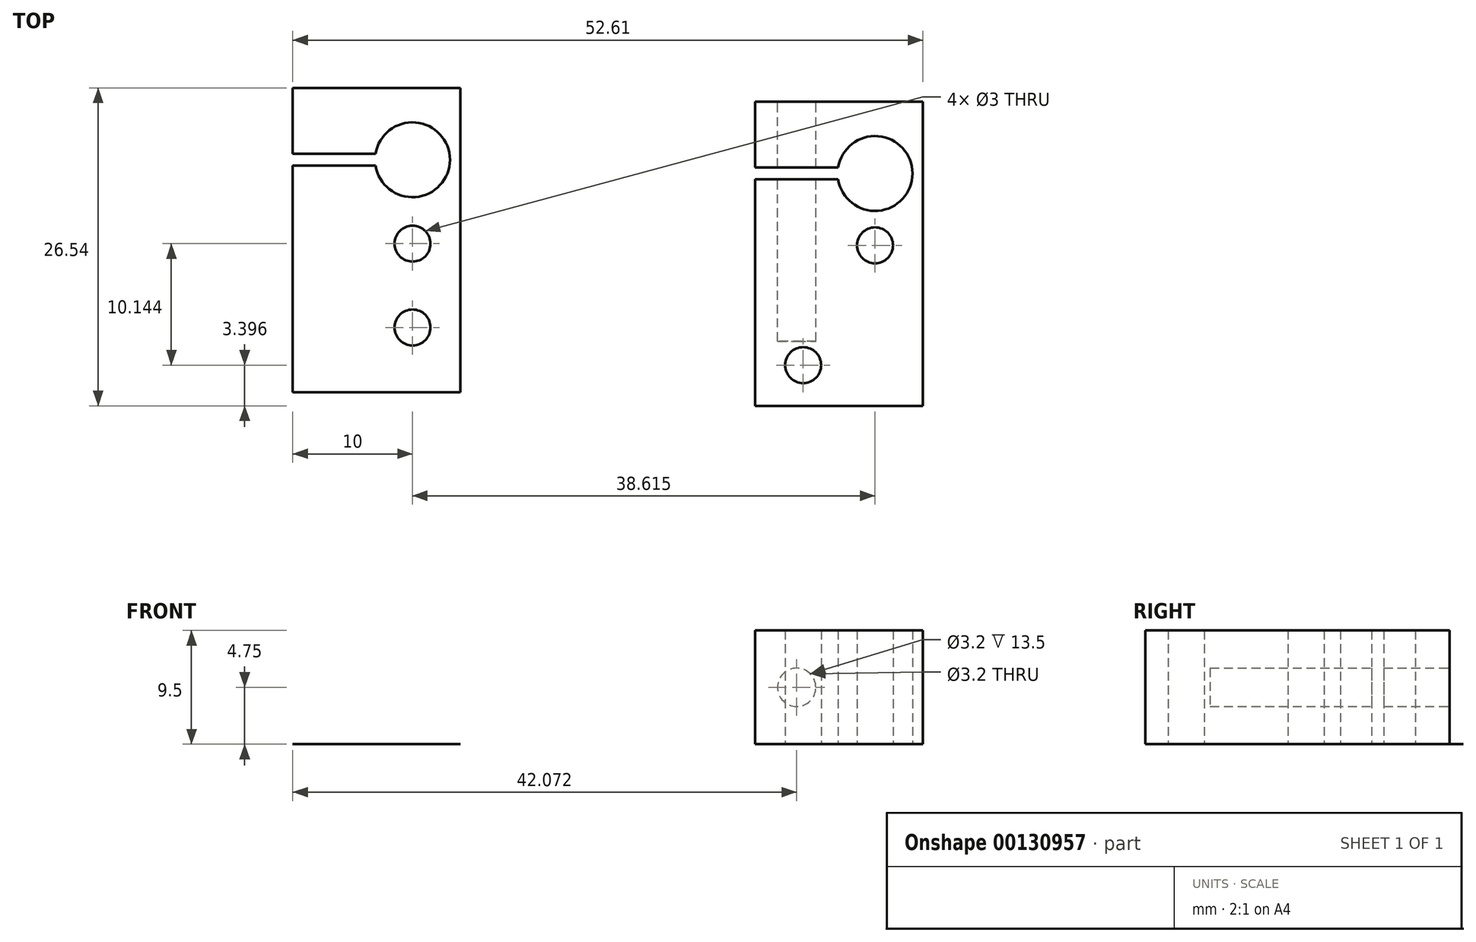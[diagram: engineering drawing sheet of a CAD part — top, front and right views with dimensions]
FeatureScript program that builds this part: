
annotation { "Feature Type Name" : "Feature", "Feature Type Description" : "" }
export const myFeature = defineFeature(function(context is Context, id is Id, definition is map)
    precondition{}
    {
        {
            var Q0;
            Q0=qCreatedBy(makeId("Top.planeOp"),FACE);
            var sketch = newSketch(context, id + "F0", { "sketchPlane" : qUnion([Q0])});
            skLineSegment(sketch, "E0.bottom", {"start": v(7, -12.7) * mm, "end": v(-7, -12.7) * mm});
            skLineSegment(sketch, "E0.top", {"start": v(7, 12.7) * mm, "end": v(-7, 12.7) * mm});
            skLineSegment(sketch, "E0.left", {"start": v(7, -12.7) * mm, "end": v(7, 12.7) * mm});
            skLineSegment(sketch, "E0.right", {"start": v(-7, -12.7) * mm, "end": v(-7, 6.2) * mm});
            skPoint(sketch, "E0.middle", {"position": v(0, 0) * mm});
            skArc(sketch, "E1", {"start": v(-0.08, 6.2) * mm, "mid": v(6.12, 6.7) * mm, "end": v(-0.08, 7.2) * mm});
            skCircle(sketch, "E2", {"center": v(3, -7.3) * mm, "radius": 1.5 * mm});
            skLineSegment(sketch, "E3.bottom", {"start": v(-5, 12.7) * mm, "end": v(-2, 12.7) * mm, "construction": true});
            skLineSegment(sketch, "E3.top", {"start": v(-5, -12.7) * mm, "end": v(-2, -12.7) * mm, "construction": true});
            skLineSegment(sketch, "E3.left", {"start": v(-5, 12.7) * mm, "end": v(-5, -12.7) * mm, "construction": true});
            skLineSegment(sketch, "E3.right", {"start": v(-2, 12.7) * mm, "end": v(-2, -12.7) * mm, "construction": true});
            skLineSegment(sketch, "E4.bottom", {"start": v(-7, 7.2) * mm, "end": v(-0.08, 7.2) * mm});
            skLineSegment(sketch, "E4.top", {"start": v(-7, 6.2) * mm, "end": v(-0.08, 6.2) * mm});
            skLineSegment(sketch, "E5.trimOffspring", {"start": v(-7, 7.2) * mm, "end": v(-7, 12.7) * mm});
            skLineSegment(sketch, "E6", {"start": v(-3.54, 6.2) * mm, "end": v(-3.54, 7.2) * mm, "construction": true});
            skCircle(sketch, "E7", {"center": v(3, -0.3) * mm, "radius": 1.5 * mm});
            skLineSegment(sketch, "E8", {"start": v(3, -7.3) * mm, "end": v(3, -0.3) * mm, "construction": true});
            skLineSegment(sketch, "E9", {"start": v(3, -0.3) * mm, "end": v(3, 6.7) * mm, "construction": true});
            skSolve(sketch);
        }
        {
            var Q0;
            Q0=qSketchRegion(id+"F0",true);
            extrude(context, id + "F1", {"entities" : qUnion([Q0]), "depth" : 3 / 203.2 * mm});
        }
        {
            var Q0;
            Q0=makeQuery(id+"F1.opExtrude","SWEPT_FACE",FACE,{"disambiguationData":[OSD([sQuery(id+"F0.wireOp",EDGE,"E0.top")])]});
            var sketch = newSketch(context, id + "F2", { "sketchPlane" : qUnion([Q0])});
            skCircle(sketch, "E10", {"center": v(3.54, 4.76) * mm, "radius": 1.25 * mm});
            skLineSegment(sketch, "E11", {"start": v(7, 4.76) * mm, "end": v(0.08, 4.76) * mm, "construction": true});
            skSolve(sketch);
        }
        {
            var Q0;
            Q0=qSketchRegion(id+"F2",true);
            extrude(context, id + "F3", {"entities" : qUnion([Q0]), "operationType" : NewBodyOperationType.REMOVE, "endBound" : BoundingType.THROUGH_ALL, "oppositeDirection" : true, "depth" : 25 * mm});
        }
        {
            var Q0;
            Q0=qCreatedBy(makeId("Top.planeOp"),FACE);
            var sketch = newSketch(context, id + "F4", { "sketchPlane" : qUnion([Q0])});
            skLineSegment(sketch, "E12.bottom", {"start": v(45.61, -13.84) * mm, "end": v(31.61, -13.84) * mm});
            skLineSegment(sketch, "E12.top", {"start": v(45.61, 11.56) * mm, "end": v(31.61, 11.56) * mm});
            skLineSegment(sketch, "E12.left", {"start": v(45.61, -13.84) * mm, "end": v(45.61, 11.56) * mm});
            skLineSegment(sketch, "E12.right", {"start": v(31.61, -13.84) * mm, "end": v(31.61, 5.06) * mm});
            skPoint(sketch, "E12.middle", {"position": v(38.61, -1.14) * mm});
            skArc(sketch, "E13", {"start": v(38.53, 5.06) * mm, "mid": v(44.74, 5.56) * mm, "end": v(38.53, 6.06) * mm});
            skCircle(sketch, "E14", {"center": v(35.61, -10.44) * mm, "radius": 1.5 * mm});
            skLineSegment(sketch, "E15.bottom", {"start": v(31.61, 6.06) * mm, "end": v(38.53, 6.06) * mm});
            skLineSegment(sketch, "E15.top", {"start": v(31.61, 5.06) * mm, "end": v(38.53, 5.06) * mm});
            skLineSegment(sketch, "E16.trimOffspring", {"start": v(31.61, 6.06) * mm, "end": v(31.61, 11.56) * mm});
            skLineSegment(sketch, "E17", {"start": v(35.07, 5.06) * mm, "end": v(35.07, 6.06) * mm, "construction": true});
            skCircle(sketch, "E18", {"center": v(41.61, -0.44) * mm, "radius": 1.5 * mm});
            skLineSegment(sketch, "E19", {"start": v(35.61, -10.44) * mm, "end": v(35.61, -13.84) * mm, "construction": true});
            skLineSegment(sketch, "E20", {"start": v(35.61, -10.44) * mm, "end": v(41.61, -10.44) * mm, "construction": true});
            skLineSegment(sketch, "E21", {"start": v(41.61, -10.44) * mm, "end": v(41.61, -0.44) * mm, "construction": true});
            skSolve(sketch);
        }
        {
            var Q0;
            Q0 = qSketchRegion(id + "F4", true);
            extrude(context, id + "F5", {"entities" : qUnion([Q0]), "depth" : 9.5 * mm});
        }
        {
            var Q0;
            Q0=makeQuery(id+"F5.opExtrude","SWEPT_FACE",FACE,{"disambiguationData":[OSD([sQuery(id+"F4.wireOp",EDGE,"E12.top")])]});
            var sketch = newSketch(context, id + "F6", { "sketchPlane" : qUnion([Q0])});
            skLineSegment(sketch, "E22", {"start": v(-38.53, 4.75) * mm, "end": v(-31.61, 4.75) * mm, "construction": true});
            skCircle(sketch, "E23", {"center": v(-35.07, 4.75) * mm, "radius": 1.6 * mm});
            skSolve(sketch);
        }
        {
            var Q0;
            Q0 = qSketchRegion(id + "F6", true);
            extrude(context, id + "F7", {"entities" : qUnion([Q0]), "operationType" : NewBodyOperationType.REMOVE, "oppositeDirection" : true, "depth" : 20 * mm});
        }
    });
